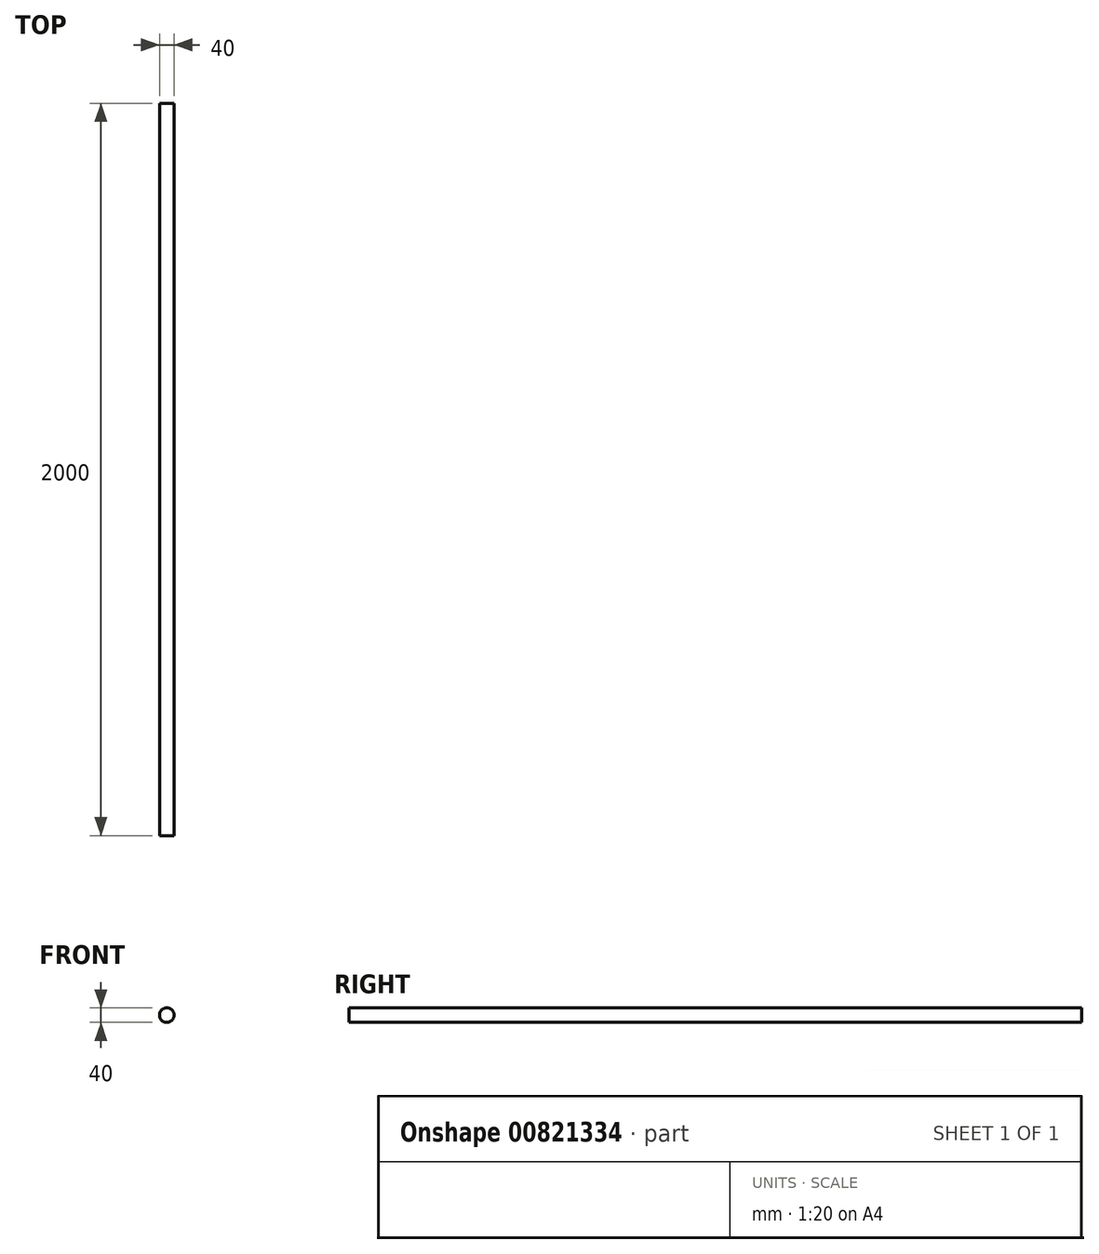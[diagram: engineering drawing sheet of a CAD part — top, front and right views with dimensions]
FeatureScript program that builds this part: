
annotation { "Feature Type Name" : "Feature", "Feature Type Description" : "" }
export const myFeature = defineFeature(function(context is Context, id is Id, definition is map)
    precondition{}
    {
        {
            var Q0;
            Q0=qCreatedBy(makeId("Front.planeOp"),FACE);
            var sketch = newSketch(context, id + "F0", { "sketchPlane" : qUnion([Q0])});
            skCircle(sketch, "E0", {"center": v(-75.06, 0) * mm, "radius": 20 * mm});
            skCircle(sketch, "E1", {"center": v(74.8, 0) * mm, "radius": 20 * mm});
            skSolve(sketch);
        }
        {
            var Q0;
            Q0=makeQuery(id+"F0.imprint","IMPRINT",FACE,{"disambiguationData":[TD([[makeQuery(id+"F0.imprint","IMPRINT",EDGE,{"derivedFrom":sQuery(id+"F0.wireOp",EDGE,"E0")}),1.0]])]});
            extrude(context, id + "F1", {"entities" : qUnion([Q0]), "depth" : 2000 * mm, "offsetDistance" : 25 * mm});
        }
    });
